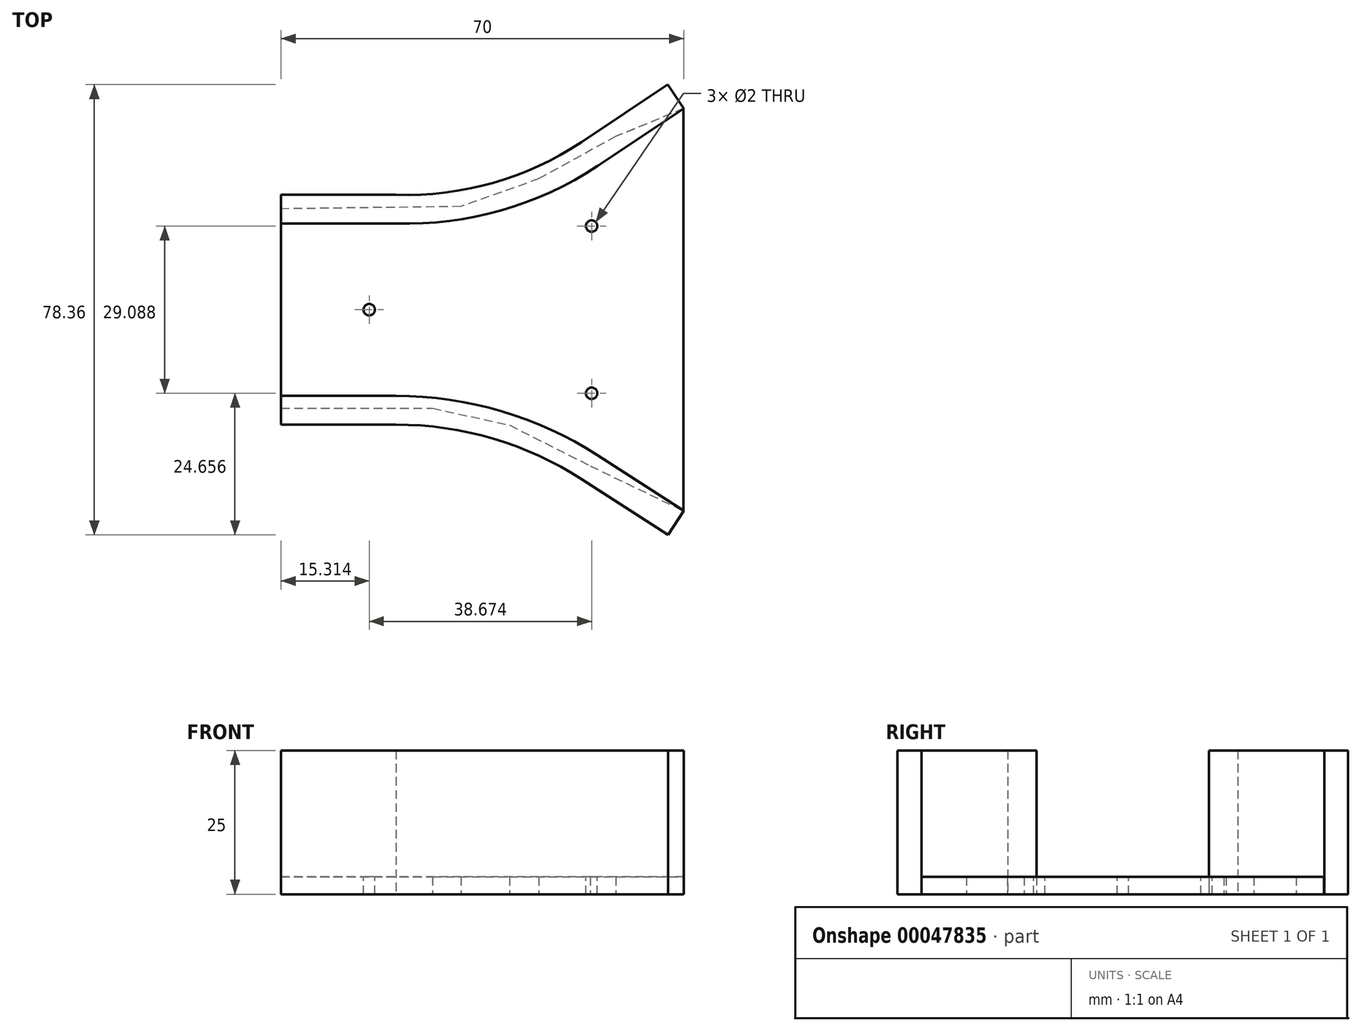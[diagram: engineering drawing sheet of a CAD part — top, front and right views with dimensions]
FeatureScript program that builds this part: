
annotation { "Feature Type Name" : "Feature", "Feature Type Description" : "" }
export const myFeature = defineFeature(function(context is Context, id is Id, definition is map)
    precondition{}
    {
        {
            var Q0;
            Q0=qCreatedBy(makeId("Top.planeOp"),FACE);
            var sketch = newSketch(context, id + "F0", { "sketchPlane" : qUnion([Q0])});
            skLineSegment(sketch, "E0", {"start": v(0, 15) * mm, "end": v(40, 15) * mm, "construction": true});
            skLineSegment(sketch, "E1", {"start": v(40, 15) * mm, "end": v(70, 35) * mm, "construction": true});
            skLineSegment(sketch, "E2", {"start": v(70, 35) * mm, "end": v(70, -35) * mm, "construction": true});
            skLineSegment(sketch, "E3", {"start": v(70, -35) * mm, "end": v(39.02, -15) * mm, "construction": true});
            skLineSegment(sketch, "E4", {"start": v(39.02, -15) * mm, "end": v(0, -15) * mm, "construction": true});
            skLineSegment(sketch, "E5", {"start": v(0, -15) * mm, "end": v(0, 15) * mm});
            skLineSegment(sketch, "E6", {"start": v(40, 38.6) * mm, "end": v(40, -30.77) * mm, "construction": true});
            skLineSegment(sketch, "E7", {"start": v(70, 35) * mm, "end": v(55, 25) * mm});
            skLineSegment(sketch, "E8", {"start": v(70, -35) * mm, "end": v(55, -25.32) * mm});
            skArc(sketch, "E9", {"start": v(55, 25) * mm, "mid": v(38.28, 17.27) * mm, "end": v(20, 15) * mm});
            skLineSegment(sketch, "E10", {"start": v(20, 39.94) * mm, "end": v(20, -33.31) * mm, "construction": true});
            skLineSegment(sketch, "E11", {"start": v(55, 46.25) * mm, "end": v(55, -47.23) * mm, "construction": true});
            skLineSegment(sketch, "E12", {"start": v(0, 15) * mm, "end": v(20, 15) * mm});
            skLineSegment(sketch, "E13", {"start": v(0, -15) * mm, "end": v(20, -15) * mm});
            skLineSegment(sketch, "E14", {"start": v(0, 20) * mm, "end": v(20, 20) * mm});
            skLineSegment(sketch, "E15", {"start": v(0, -20) * mm, "end": v(20, -20) * mm});
            skLineSegment(sketch, "E16", {"start": v(70, 35) * mm, "end": v(64.45, 43.32) * mm, "construction": true});
            skLineSegment(sketch, "E17", {"start": v(70, -35) * mm, "end": v(60.38, -49.9) * mm, "construction": true});
            skLineSegment(sketch, "E18", {"start": v(55, 25) * mm, "end": v(50.98, 31.03) * mm, "construction": true});
            skLineSegment(sketch, "E19", {"start": v(55, -25.32) * mm, "end": v(51.47, -30.78) * mm, "construction": true});
            skLineSegment(sketch, "E20", {"start": v(67.23, 39.16) * mm, "end": v(52.23, 29.16) * mm});
            skLineSegment(sketch, "E21", {"start": v(67.29, -39.2) * mm, "end": v(52.29, -29.52) * mm});
            skLineSegment(sketch, "E22", {"start": v(70, 35) * mm, "end": v(67.23, 39.16) * mm});
            skLineSegment(sketch, "E23", {"start": v(70, -35) * mm, "end": v(67.29, -39.2) * mm});
            skLineSegment(sketch, "E24", {"start": v(0, 20) * mm, "end": v(0, 15) * mm});
            skLineSegment(sketch, "E25", {"start": v(0, -15) * mm, "end": v(0, -20) * mm});
            skArc(sketch, "E26", {"start": v(52.23, 29.16) * mm, "mid": v(36.83, 22.05) * mm, "end": v(20, 20) * mm});
            skArc(sketch, "E27", {"start": v(55, -25.32) * mm, "mid": v(38.24, -17.63) * mm, "end": v(20, -15) * mm});
            skArc(sketch, "E28", {"start": v(52.29, -29.52) * mm, "mid": v(36.83, -22.43) * mm, "end": v(20, -20) * mm});
            skLineSegment(sketch, "E29", {"start": v(70, 35) * mm, "end": v(0, 35) * mm, "construction": true});
            skLineSegment(sketch, "E30", {"start": v(70, -35) * mm, "end": v(0, -35) * mm, "construction": true});
            skSolve(sketch);
        }
        {
            var Q0;
            Q0=qSketchRegion(id+"F0",true);
            extrude(context, id + "F1", {"entities" : qUnion([Q0]), "depth" : 25 * mm});
        }
        {
            var Q0;
            Q0=qCreatedBy(makeId("Top.planeOp"),FACE);
            var sketch = newSketch(context, id + "F2", { "sketchPlane" : qUnion([Q0])});
            skLineSegment(sketch, "E31", {"start": v(0, 17.54) * mm, "end": v(0, -17.14) * mm});
            skLineSegment(sketch, "E32", {"start": v(0, -17.14) * mm, "end": v(26.32, -17.14) * mm});
            skLineSegment(sketch, "E33", {"start": v(26.32, -17.14) * mm, "end": v(39.7, -20.09) * mm});
            skLineSegment(sketch, "E34", {"start": v(39.7, -20.09) * mm, "end": v(53.77, -27.19) * mm});
            skLineSegment(sketch, "E35", {"start": v(53.77, -27.19) * mm, "end": v(69.98, -35) * mm});
            skLineSegment(sketch, "E36", {"start": v(69.98, -35) * mm, "end": v(69.98, 34.97) * mm});
            skLineSegment(sketch, "E37", {"start": v(69.98, 34.97) * mm, "end": v(58.2, 30.13) * mm});
            skLineSegment(sketch, "E38", {"start": v(58.2, 30.13) * mm, "end": v(44.8, 22.77) * mm});
            skLineSegment(sketch, "E39", {"start": v(44.8, 22.77) * mm, "end": v(31.27, 17.95) * mm});
            skLineSegment(sketch, "E40", {"start": v(31.27, 17.95) * mm, "end": v(0, 17.54) * mm});
            skSolve(sketch);
        }
        {
            var Q0;
            Q0=qSketchRegion(id+"F2",true);
            extrude(context, id + "F3", {"entities" : qUnion([Q0]), "depth" : 3 * mm});
        }
        {
            var Q0;
            Q0=makeQuery(id+"F3.opExtrude","CAP_FACE",FACE,{"disambiguationData":[OSD([sQuery(id+"F2.wireOp",EDGE,"E31"),sQuery(id+"F2.wireOp",EDGE,"E32"),sQuery(id+"F2.wireOp",EDGE,"E33"),sQuery(id+"F2.wireOp",EDGE,"E34"),sQuery(id+"F2.wireOp",EDGE,"E35"),sQuery(id+"F2.wireOp",EDGE,"E36"),sQuery(id+"F2.wireOp",EDGE,"E37"),sQuery(id+"F2.wireOp",EDGE,"E38"),sQuery(id+"F2.wireOp",EDGE,"E39"),sQuery(id+"F2.wireOp",EDGE,"E40")])],"isStart":false});
            var sketch = newSketch(context, id + "F4", { "sketchPlane" : qUnion([Q0])});
            skCircle(sketch, "E41", {"center": v(15.31, 0) * mm, "radius": 1 * mm});
            skLineSegment(sketch, "E42", {"start": v(53.99, 17.16) * mm, "end": v(53.99, -21.37) * mm, "construction": true});
            skCircle(sketch, "E43", {"center": v(53.99, 14.54) * mm, "radius": 1 * mm});
            skCircle(sketch, "E44", {"center": v(53.99, -14.54) * mm, "radius": 1 * mm});
            skSolve(sketch);
        }
        {
            var Q0;
            Q0=qSketchRegion(id+"F4",true);
            extrude(context, id + "F5", {"entities" : qUnion([Q0]), "operationType" : NewBodyOperationType.REMOVE, "oppositeDirection" : true, "depth" : 3 * mm});
        }
    });
